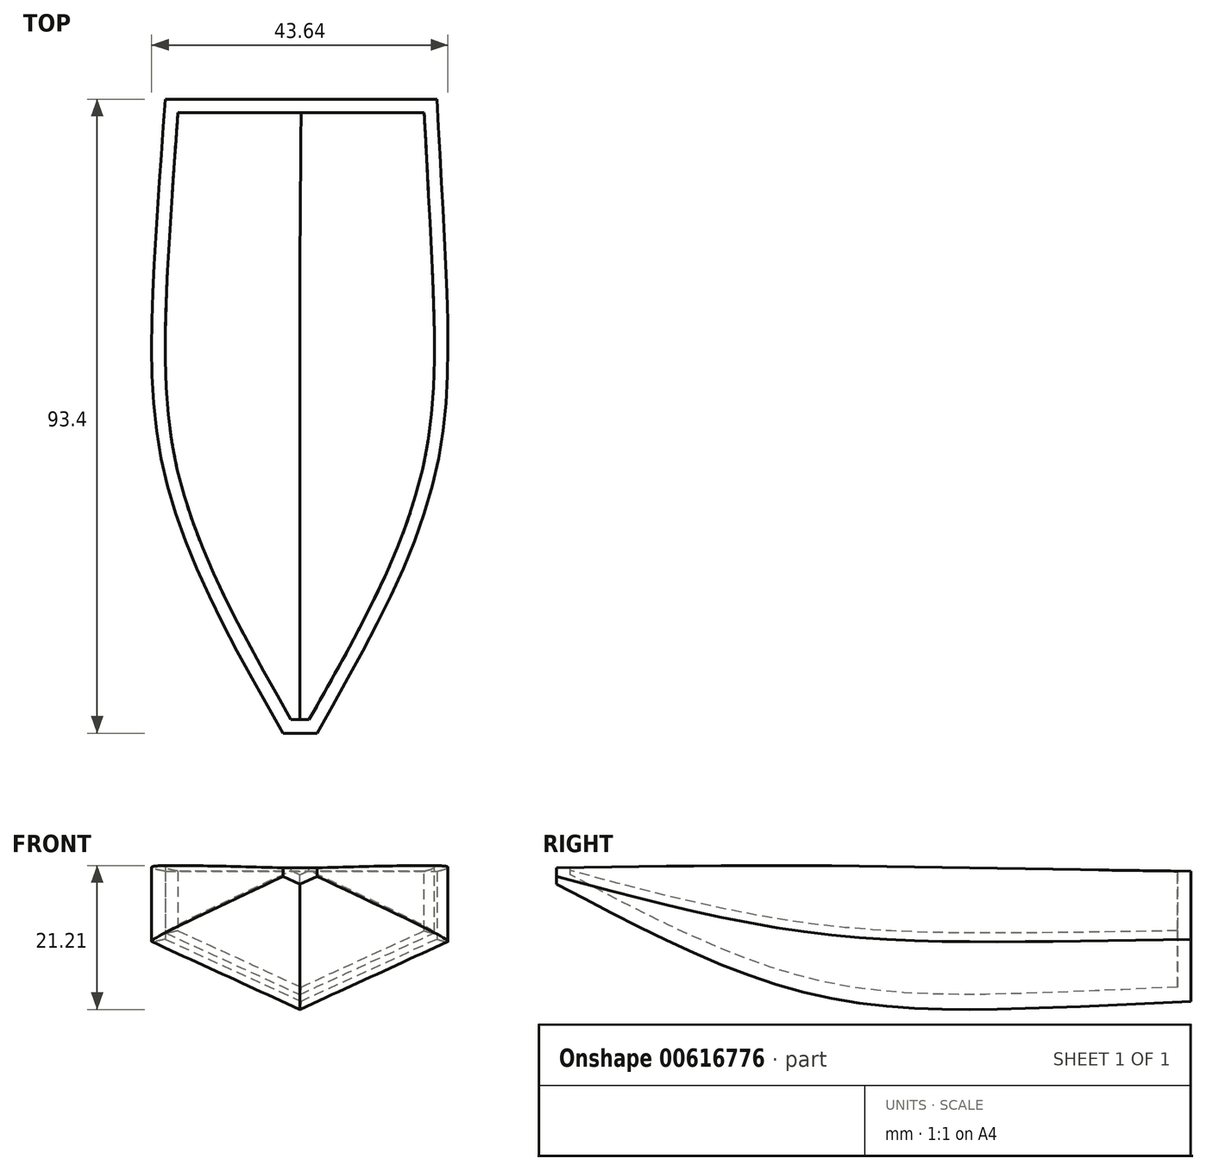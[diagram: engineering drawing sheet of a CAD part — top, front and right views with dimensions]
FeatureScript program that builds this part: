
annotation { "Feature Type Name" : "Feature", "Feature Type Description" : "" }
export const myFeature = defineFeature(function(context is Context, id is Id, definition is map)
    precondition{}
    {
        {
            var Q0;
            Q0=qCreatedBy(makeId("Front.planeOp"),FACE);
            cPlane(context, id + "F0", {"entities" : qUnion([Q0]), "cplaneType" : CPlaneType.OFFSET, "offset" : 38.4 * mm, "width" : 150 * mm, "height" : 150 * mm});
        }
        {
            var Q0;
            Q0=qCreatedBy(makeId("Front.planeOp"),FACE);
            cPlane(context, id + "F1", {"entities" : qUnion([Q0]), "cplaneType" : CPlaneType.OFFSET, "offset" : 29.5 * mm, "oppositeDirection" : true, "width" : 150 * mm, "height" : 150 * mm});
        }
        {
            var Q0;
            Q0=qCreatedBy(id+"F0.planeOp",FACE);
            var sketch = newSketch(context, id + "F2", { "sketchPlane" : qUnion([Q0])});
            skLineSegment(sketch, "E0", {"start": v(-2.5, -0.02) * mm, "end": v(2.5, -0.02) * mm});
            skLineSegment(sketch, "E1", {"start": v(2.5, -0.02) * mm, "end": v(2.5, -1.27) * mm});
            skLineSegment(sketch, "E2", {"start": v(-2.5, -0.02) * mm, "end": v(-2.5, -1.27) * mm});
            skLineSegment(sketch, "E3", {"start": v(-2.5, -1.27) * mm, "end": v(0, -2.41) * mm});
            skLineSegment(sketch, "E4", {"start": v(2.5, -1.27) * mm, "end": v(0, -2.41) * mm});
            skSolve(sketch);
        }
        {
            var Q0;
            Q0=qCreatedBy(makeId("Front.planeOp"),FACE);
            var sketch = newSketch(context, id + "F3", { "sketchPlane" : qUnion([Q0])});
            skLineSegment(sketch, "E5", {"start": v(-20, 0.31) * mm, "end": v(20, 0.31) * mm});
            skLineSegment(sketch, "E6", {"start": v(20, 0.31) * mm, "end": v(20, -9.69) * mm});
            skLineSegment(sketch, "E7", {"start": v(-20, 0.31) * mm, "end": v(-20, -9.69) * mm});
            skLineSegment(sketch, "E8", {"start": v(-20, -9.69) * mm, "end": v(0, -18.85) * mm});
            skLineSegment(sketch, "E9", {"start": v(20, -9.69) * mm, "end": v(0, -18.85) * mm});
            skSolve(sketch);
        }
        {
            var Q0;
            Q0=qCreatedBy(id+"F1.planeOp",FACE);
            var sketch = newSketch(context, id + "F4", { "sketchPlane" : qUnion([Q0])});
            skLineSegment(sketch, "E10", {"start": v(-21.5, -0.14) * mm, "end": v(21.5, -0.14) * mm});
            skLineSegment(sketch, "E11", {"start": v(21.5, -0.14) * mm, "end": v(21.5, -10.9) * mm});
            skLineSegment(sketch, "E12", {"start": v(-21.5, -0.14) * mm, "end": v(-21.5, -10.9) * mm});
            skLineSegment(sketch, "E13", {"start": v(-21.5, -10.9) * mm, "end": v(0, -20.75) * mm});
            skLineSegment(sketch, "E14", {"start": v(21.5, -10.9) * mm, "end": v(0, -20.75) * mm});
            skSolve(sketch);
        }
        {
            var Q0;
            Q0=qCreatedBy(makeId("Front.planeOp"),FACE);
            cPlane(context, id + "F5", {"entities" : qUnion([Q0]), "cplaneType" : CPlaneType.OFFSET, "offset" : 55 * mm, "oppositeDirection" : true, "width" : 150 * mm, "height" : 150 * mm});
        }
        {
            var Q0;
            Q0=qCreatedBy(id+"F5.planeOp",FACE);
            var sketch = newSketch(context, id + "F6", { "sketchPlane" : qUnion([Q0])});
            skLineSegment(sketch, "E15", {"start": v(-19.82, -0.52) * mm, "end": v(20.18, -0.52) * mm});
            skLineSegment(sketch, "E16", {"start": v(20.18, -0.52) * mm, "end": v(20.18, -10.52) * mm});
            skLineSegment(sketch, "E17", {"start": v(-19.82, -0.52) * mm, "end": v(-19.82, -10.52) * mm});
            skLineSegment(sketch, "E18", {"start": v(-19.82, -10.52) * mm, "end": v(0.18, -19.69) * mm});
            skLineSegment(sketch, "E19", {"start": v(20.18, -10.52) * mm, "end": v(0.18, -19.69) * mm});
            skSolve(sketch);
        }
        {
            var Q0;
            Q0 = qSketchRegion(id + "F6", true);
            var Q1;
            Q1 = qSketchRegion(id + "F4", true);
            var Q2;
            Q2 = qSketchRegion(id + "F3", true);
            var Q3;
            Q3 = qSketchRegion(id + "F2", true);
            loft(context, id + "F7", {"sheetProfilesArray" : [{ "sheetProfileEntities" : qUnion([Q0]) }, { "sheetProfileEntities" : qUnion([Q1]) }, { "sheetProfileEntities" : qUnion([Q2]) }, { "sheetProfileEntities" : qUnion([Q3]) }]});
        }
        {
            var Q0;
            Q0=makeQuery(id+"F7.opLoft","SWEPT_FACE",FACE,{"disambiguationData":[OSD([sQuery(id+"F4.wireOp",EDGE,"E10"),sQuery(id+"F4.wireOp",EDGE,"E11"),sQuery(id+"F4.wireOp",EDGE,"E12"),sQuery(id+"F6.wireOp",EDGE,"E15"),sQuery(id+"F6.wireOp",EDGE,"E16"),sQuery(id+"F6.wireOp",EDGE,"E17")])]});
            shell(context, id + "F8", {"entities" : qUnion([Q0]), "thickness" : 2 * mm});
        }
    });
